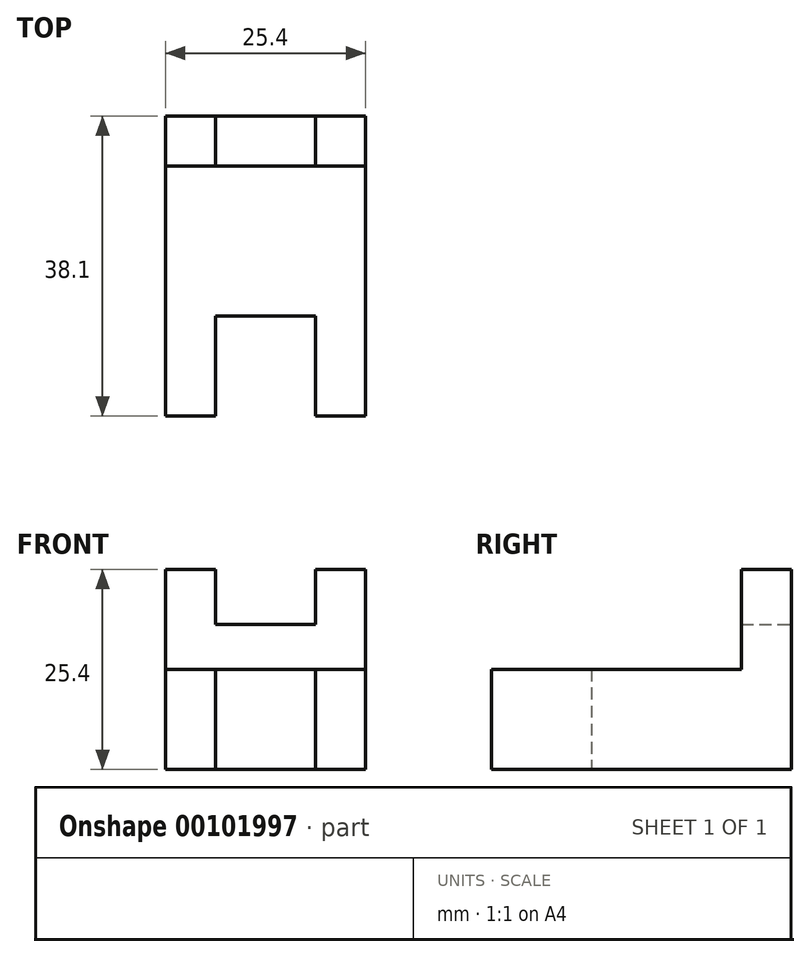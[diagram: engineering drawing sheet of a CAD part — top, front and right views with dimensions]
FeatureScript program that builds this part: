
annotation { "Feature Type Name" : "Feature", "Feature Type Description" : "" }
export const myFeature = defineFeature(function(context is Context, id is Id, definition is map)
    precondition{}
    {
        {
            var Q0;
            Q0=qCreatedBy(makeId("Top.planeOp"),FACE);
            var sketch = newSketch(context, id + "F0", { "sketchPlane" : qUnion([Q0])});
            skLineSegment(sketch, "E0", {"start": v(0, 0) * mm, "end": v(0, -38.1) * mm});
            skLineSegment(sketch, "E1", {"start": v(0, -38.1) * mm, "end": v(6.35, -38.1) * mm});
            skLineSegment(sketch, "E2", {"start": v(6.35, -38.1) * mm, "end": v(6.35, -25.4) * mm});
            skLineSegment(sketch, "E3", {"start": v(6.35, -25.4) * mm, "end": v(19.05, -25.4) * mm});
            skLineSegment(sketch, "E4", {"start": v(19.05, -25.4) * mm, "end": v(19.05, -38.1) * mm});
            skLineSegment(sketch, "E5", {"start": v(19.05, -38.1) * mm, "end": v(25.4, -38.1) * mm});
            skLineSegment(sketch, "E6", {"start": v(25.4, -38.1) * mm, "end": v(25.4, 0) * mm});
            skLineSegment(sketch, "E7", {"start": v(25.4, 0) * mm, "end": v(0, 0) * mm});
            skSolve(sketch);
        }
        {
            var Q0;
            Q0 = qSketchRegion(id + "F0", true);
            extrude(context, id + "F1", {"entities" : qUnion([Q0]), "depth" : 12.7 * mm});
        }
        {
            var Q0;
            Q0=qCreatedBy(makeId("Top.planeOp"),FACE);
            var sketch = newSketch(context, id + "F2", { "sketchPlane" : qUnion([Q0])});
            skLineSegment(sketch, "E8", {"start": v(25.4, 0) * mm, "end": v(25.4, -6.35) * mm});
            skLineSegment(sketch, "E9", {"start": v(25.4, -6.35) * mm, "end": v(19.05, -6.35) * mm});
            skLineSegment(sketch, "E10", {"start": v(19.05, -6.35) * mm, "end": v(19.05, 0) * mm});
            skLineSegment(sketch, "E11", {"start": v(19.05, 0) * mm, "end": v(25.4, 0) * mm});
            skLineSegment(sketch, "E12", {"start": v(0, 0) * mm, "end": v(6.35, 0) * mm});
            skLineSegment(sketch, "E13", {"start": v(6.35, 0) * mm, "end": v(6.35, -6.35) * mm});
            skLineSegment(sketch, "E14", {"start": v(6.35, -6.35) * mm, "end": v(0, -6.35) * mm});
            skLineSegment(sketch, "E15", {"start": v(0, -6.35) * mm, "end": v(0, 0) * mm});
            skSolve(sketch);
        }
        {
            var Q0;
            Q0 = qSketchRegion(id + "F2", true);
            extrude(context, id + "F3", {"entities" : qUnion([Q0]), "operationType" : NewBodyOperationType.ADD, "depth" : 25.4 * mm});
        }
        {
            var Q0;
            Q0=qCreatedBy(makeId("Front.planeOp"),FACE);
            var sketch = newSketch(context, id + "F4", { "sketchPlane" : qUnion([Q0])});
            skLineSegment(sketch, "E16", {"start": v(6.35, 18.44) * mm, "end": v(19.05, 18.44) * mm});
            skLineSegment(sketch, "E17", {"start": v(19.05, 18.44) * mm, "end": v(19.05, 12.1) * mm});
            skLineSegment(sketch, "E18", {"start": v(19.05, 12.1) * mm, "end": v(6.35, 12.1) * mm});
            skLineSegment(sketch, "E19", {"start": v(6.35, 12.1) * mm, "end": v(6.35, 18.44) * mm});
            skSolve(sketch);
        }
        {
            var Q0;
            Q0 = qSketchRegion(id + "F4", true);
            extrude(context, id + "F5", {"entities" : qUnion([Q0]), "operationType" : NewBodyOperationType.ADD, "depth" : 6.35 * mm});
        }
    });
